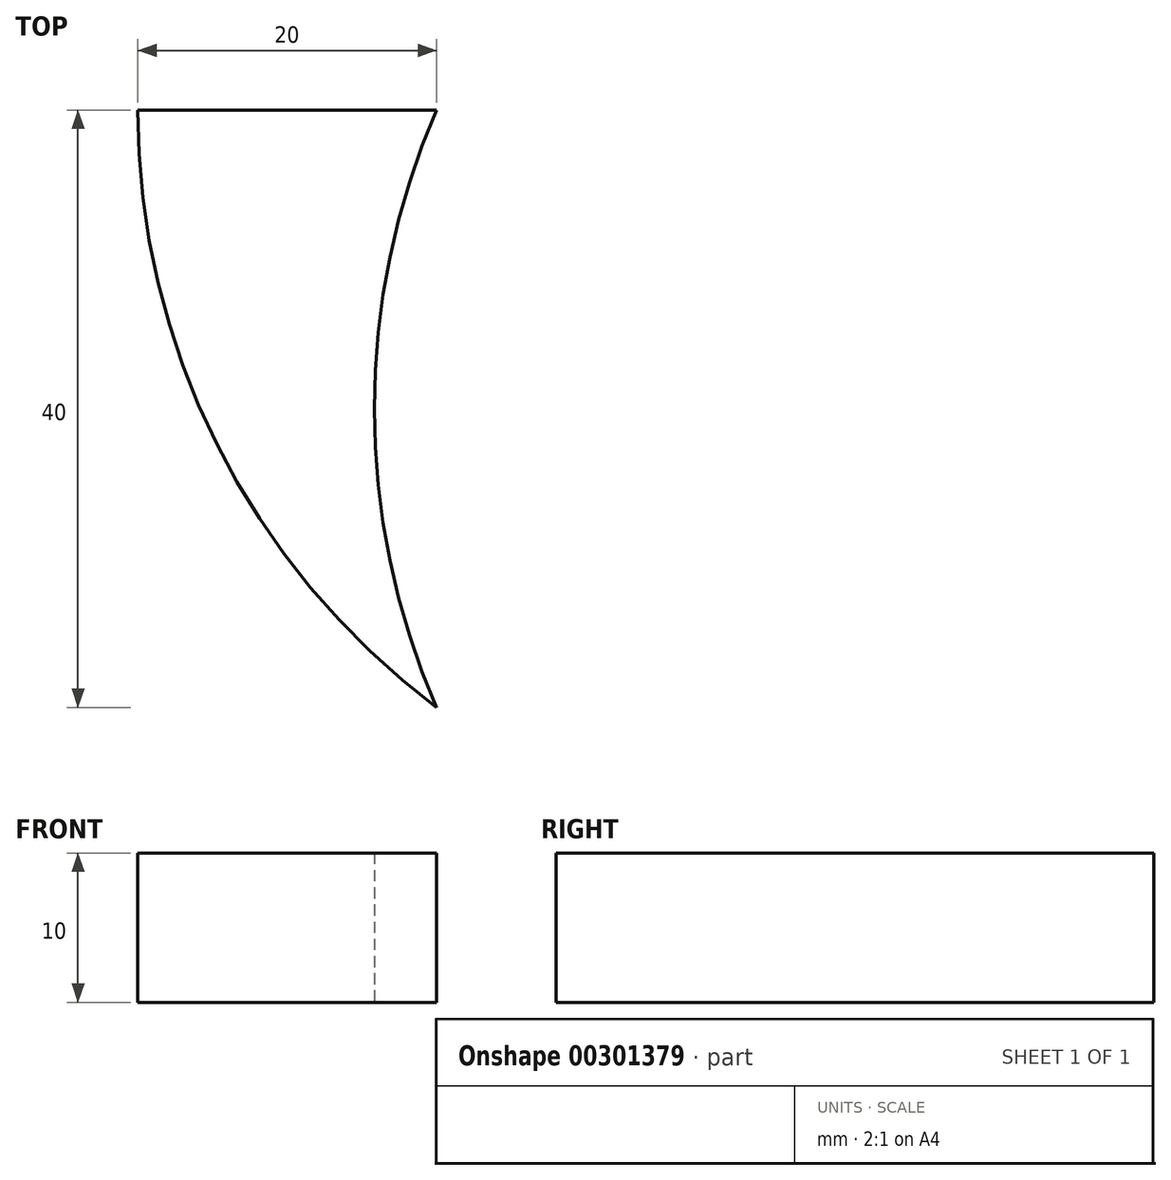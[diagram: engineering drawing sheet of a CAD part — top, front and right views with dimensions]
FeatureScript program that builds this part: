
annotation { "Feature Type Name" : "Feature", "Feature Type Description" : "" }
export const myFeature = defineFeature(function(context is Context, id is Id, definition is map)
    precondition{}
    {
        {
            var Q0;
            Q0=qCreatedBy(makeId("Top.planeOp"),FACE);
            var sketch = newSketch(context, id + "F0", { "sketchPlane" : qUnion([Q0])});
            skArc(sketch, "E0", {"start": v(0, 40) * mm, "mid": v(-4.17, 20) * mm, "end": v(0, 0) * mm});
            skArc(sketch, "E1", {"start": v(-20, 40) * mm, "mid": v(-14.72, 17.64) * mm, "end": v(0, 0) * mm});
            skLineSegment(sketch, "E2", {"start": v(-20, 40) * mm, "end": v(0, 40) * mm});
            skSolve(sketch);
        }
        {
            var Q0;
            Q0 = qSketchRegion(id + "F0", true);
            extrude(context, id + "F1", {"entities" : qUnion([Q0]), "depth" : 10 * mm});
        }
    });
